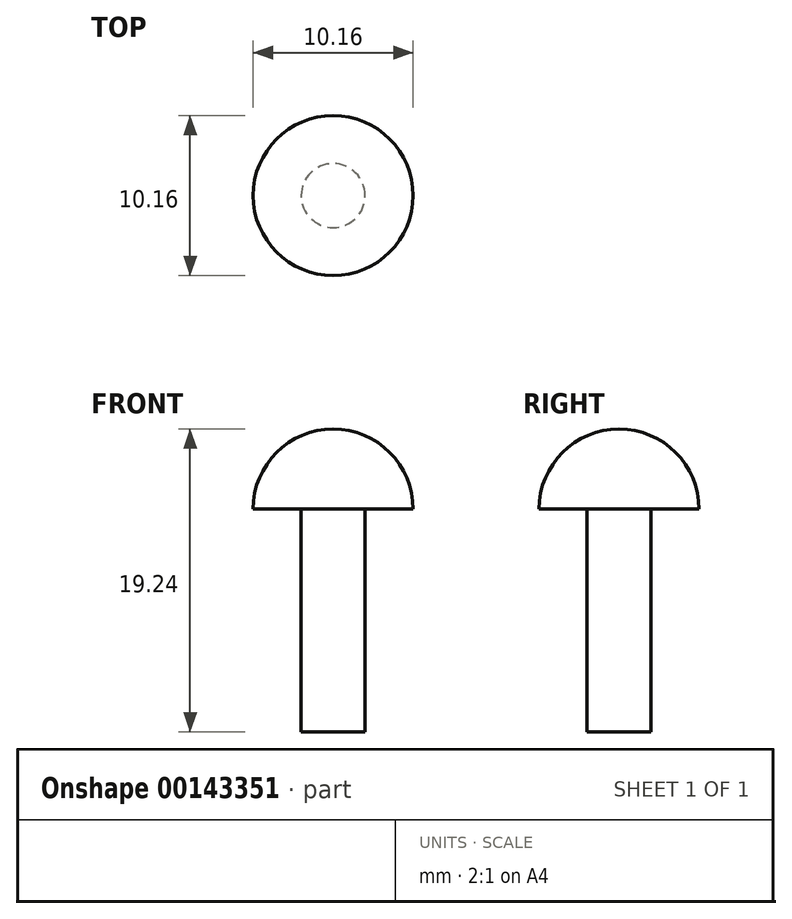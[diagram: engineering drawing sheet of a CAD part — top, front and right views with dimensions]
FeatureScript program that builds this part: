
annotation { "Feature Type Name" : "Feature", "Feature Type Description" : "" }
export const myFeature = defineFeature(function(context is Context, id is Id, definition is map)
    precondition{}
    {
        {
            var Q0;
            Q0=qCreatedBy(makeId("Top.planeOp"),FACE);
            var sketch = newSketch(context, id + "F0", { "sketchPlane" : qUnion([Q0])});
            skArc(sketch, "E0", {"start": v(5.08, 0) * mm, "mid": v(0, 5.08) * mm, "end": v(-5.08, 0) * mm});
            skLineSegment(sketch, "E1", {"start": v(-5.08, 0) * mm, "end": v(5.08, 0) * mm});
            skSolve(sketch);
        }
        {
            var Q0;
            Q0=makeQuery(id+"F0.imprint","IMPRINT",FACE,{"disambiguationData":[TD([[makeQuery(id+"F0.imprint","IMPRINT",EDGE,{"derivedFrom":sQuery(id+"F0.wireOp",EDGE,"E0")}),1.0]])]});
            var Q1;
            Q1=sQuery(id+"F0.wireOp",EDGE,"E1");
            revolve(context, id + "F1", {"entities" : qUnion([Q0]), "axis" : qUnion([Q1]), "revolveType" : RevolveType.ONE_DIRECTION, "angle" : 180 * degree});
        }
        {
            var Q0;
            Q0=makeQuery(id+"F1.opRevolve","CAP_FACE",FACE,{"disambiguationData":[OSD([sQuery(id+"F0.wireOp",EDGE,"E0"),sQuery(id+"F0.wireOp",EDGE,"E1")])],"isStart":true});
            var sketch = newSketch(context, id + "F2", { "sketchPlane" : qUnion([Q0])});
            skCircle(sketch, "E2", {"center": v(0, 0) * mm, "radius": 2.03 * mm});
            skSolve(sketch);
        }
        {
            var Q0;
            Q0=makeQuery(id+"F2.imprint","IMPRINT",FACE,{"disambiguationData":[TD([[makeQuery(id+"F2.imprint","IMPRINT",EDGE,{"derivedFrom":sQuery(id+"F2.wireOp",EDGE,"E2")}),1.0]])]});
            var Q1;
            Q1=sQuery(id+"F2.wireOp",EDGE,"E2");
            extrude(context, id + "F3", {"entities" : qUnion([Q0]), "operationType" : NewBodyOperationType.ADD, "surfaceEntities" : qUnion([Q1]), "depth" : 10.16 * mm + 4 * mm});
        }
    });
